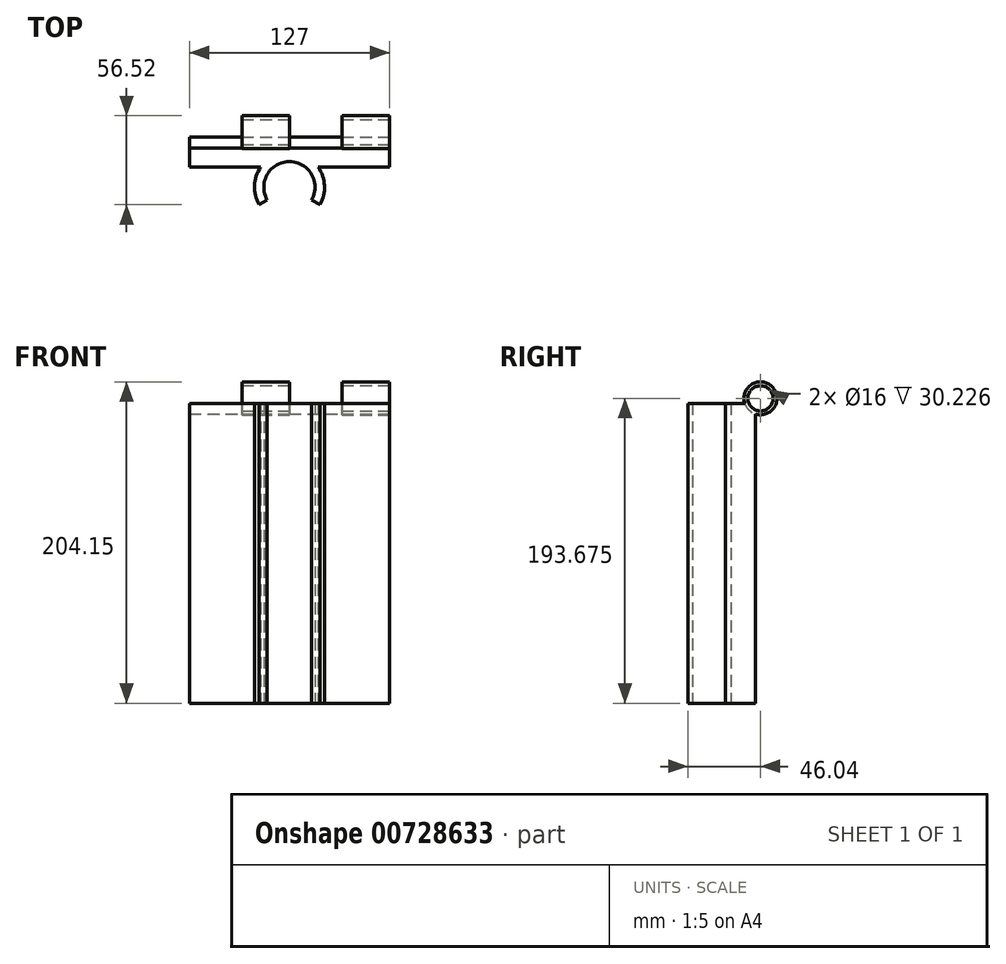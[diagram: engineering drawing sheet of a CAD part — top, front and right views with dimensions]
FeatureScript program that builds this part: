
annotation { "Feature Type Name" : "Feature", "Feature Type Description" : "" }
export const myFeature = defineFeature(function(context is Context, id is Id, definition is map)
    precondition{}
    {
        {
            var Q0;
            Q0=qCreatedBy(makeId("Front.planeOp"),FACE);
            var sketch = newSketch(context, id + "F0", { "sketchPlane" : qUnion([Q0])});
            skLineSegment(sketch, "E0.bottom", {"start": v(-63.5, 95.25) * mm, "end": v(63.5, 95.25) * mm});
            skLineSegment(sketch, "E0.top", {"start": v(-63.5, -95.25) * mm, "end": v(63.5, -95.25) * mm});
            skLineSegment(sketch, "E0.left", {"start": v(-63.5, 95.25) * mm, "end": v(-63.5, -95.25) * mm});
            skLineSegment(sketch, "E0.right", {"start": v(63.5, 95.25) * mm, "end": v(63.5, -95.25) * mm});
            skPoint(sketch, "E0.middle", {"position": v(0, 0) * mm});
            skSolve(sketch);
        }
        {
            var Q0;
            Q0 = qSketchRegion(id + "F0", true);
            extrude(context, id + "F1", {"entities" : qUnion([Q0]), "endBound" : BoundingType.SYMMETRIC, "depth" : 19.05 * mm, "offsetDistance" : 25.4 * mm});
        }
        {
            var Q0;
            Q0=qCreatedBy(makeId("Top.planeOp"),FACE);
            var sketch = newSketch(context, id + "F2", { "sketchPlane" : qUnion([Q0])});
            skArc(sketch, "E1", {"start": v(19.25, -33.34) * mm, "mid": v(0, 0) * mm, "end": v(-19.25, -33.34) * mm});
            skArc(sketch, "E2", {"start": v(14.1, -30.36) * mm, "mid": v(0, -5.95) * mm, "end": v(-14.1, -30.36) * mm});
            skLineSegment(sketch, "E3", {"start": v(0, -22.23) * mm, "end": v(-39.65, -45.12) * mm});
            skLineSegment(sketch, "E4", {"start": v(0, -22.23) * mm, "end": v(37.1, -43.64) * mm});
            skSolve(sketch);
        }
        {
            var Q0;
            {var subQ0=sQuery(id+"F2.wireOp",EDGE,"E1");Q0=makeQuery(id+"F2.imprint","IMPRINT",FACE,{"disambiguationData":[TD([[makeQuery(id+"F2.imprint","IMPRINT",EDGE,{"derivedFrom":subQ0}),1.0]])]});}
            var Q1;
            {var subQ0=sQuery(id+"F2.wireOp",EDGE,"E2");Q1=makeQuery(id+"F2.imprint","IMPRINT",FACE,{"disambiguationData":[TD([[makeQuery(id+"F2.imprint","IMPRINT",EDGE,{"derivedFrom":subQ0}),1.0]])]});}
            extrude(context, id + "F3", {"entities" : qUnion([Q0, Q1]), "operationType" : NewBodyOperationType.REMOVE, "endBound" : BoundingType.THROUGH_ALL, "depth" : 25.4 * mm, "offsetDistance" : 25.4 * mm, "hasSecondDirection" : true, "secondDirectionBound" : SecondDirectionBoundingType.THROUGH_ALL, "secondDirectionOppositeDirection" : true, "secondDirectionDepth" : 25.4 * mm});
        }
        {
            var Q0;
            {var subQ0=sQuery(id+"F2.wireOp",EDGE,"E1");Q0=makeQuery(id+"F2.imprint","IMPRINT",FACE,{"disambiguationData":[TD([[makeQuery(id+"F2.imprint","IMPRINT",EDGE,{"derivedFrom":subQ0}),1.0]])]});}
            extrude(context, id + "F4", {"entities" : qUnion([Q0]), "operationType" : NewBodyOperationType.ADD, "endBound" : BoundingType.SYMMETRIC, "depth" : 190.5 * mm, "offsetDistance" : 25.4 * mm});
        }
        {
            var Q0;
            Q0=qCreatedBy(makeId("Right.planeOp"),FACE);
            var sketch = newSketch(context, id + "F5", { "sketchPlane" : qUnion([Q0])});
            skCircle(sketch, "E5", {"center": v(12.7, 98.43) * mm, "radius": 10.48 * mm});
            skCircle(sketch, "E6", {"center": v(12.7, 98.43) * mm, "radius": 8 * mm});
            skSolve(sketch);
        }
        {
            var Q0;
            Q0 = qSketchRegion(id + "F5", true);
            var Q1;
            Q1=makeQuery(id+"F5.imprint","IMPRINT",FACE,{"disambiguationData":[TD([[makeQuery(id+"F5.imprint","IMPRINT",EDGE,{"derivedFrom":sQuery(id+"F5.wireOp",EDGE,"E6")}),1.0]])]});
            extrude(context, id + "F6", {"entities" : qUnion([Q0, Q1]), "operationType" : NewBodyOperationType.REMOVE, "endBound" : BoundingType.THROUGH_ALL, "oppositeDirection" : true, "depth" : 25.4 * mm, "offsetDistance" : 25.4 * mm, "hasSecondDirection" : true, "secondDirectionBound" : SecondDirectionBoundingType.THROUGH_ALL, "secondDirectionOppositeDirection" : false, "secondDirectionDepth" : 25.4 * mm});
        }
        {
            var Q0;
            Q0 = qSketchRegion(id + "F5", true);
            var Q1;
            Q1=makeQuery(id+"F1.opExtrude","SWEPT_FACE",FACE,{"disambiguationData":[OSD([sQuery(id+"F0.wireOp",EDGE,"E0.right")])]});
            extrude(context, id + "F7", {"entities" : qUnion([Q0]), "operationType" : NewBodyOperationType.ADD, "oppositeDirection" : true, "depth" : 30.23 * mm, "offsetDistance" : 25.4 * mm});
        }
        {
            var Q0;
            {var subQ0=sQuery(id+"F0.wireOp",EDGE,"E0.right");Q0=makeQuery(id+"F7.boolean.opBoolean","MERGE",FACE,{"derivedFrom":[makeQuery(id+"F1.opExtrude","SWEPT_FACE",FACE,{"disambiguationData":[OSD([subQ0])]}),makeQuery(id+"F7.opExtrude","CAP_FACE",FACE,{"disambiguationData":[OSD([subQ0])],"isStart":true})]});}
            var sketch = newSketch(context, id + "F8", { "sketchPlane" : qUnion([Q0])});
            skCircle(sketch, "E7", {"center": v(12.7, 98.42) * mm, "radius": 10.48 * mm});
            skCircle(sketch, "E8", {"center": v(12.7, 98.42) * mm, "radius": 8 * mm});
            skSolve(sketch);
        }
        {
            var Q0;
            Q0 = qSketchRegion(id + "F8", true);
            extrude(context, id + "F9", {"entities" : qUnion([Q0]), "operationType" : NewBodyOperationType.ADD, "oppositeDirection" : true, "depth" : 30.23 * mm, "offsetDistance" : 25.4 * mm});
        }
    });
